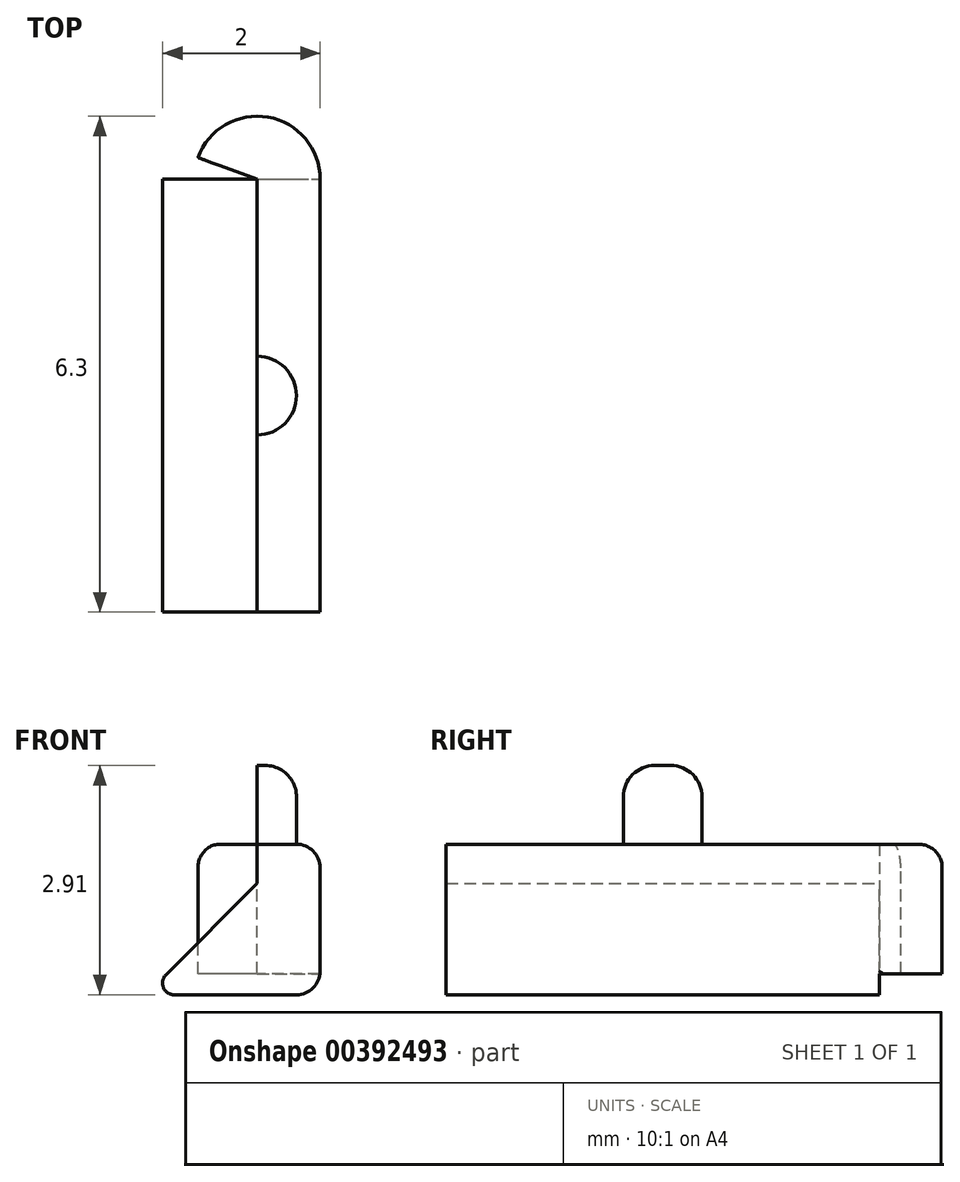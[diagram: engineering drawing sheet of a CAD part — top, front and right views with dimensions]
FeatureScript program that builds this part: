
annotation { "Feature Type Name" : "Feature", "Feature Type Description" : "" }
export const myFeature = defineFeature(function(context is Context, id is Id, definition is map)
    precondition{}
    {
        {
            var Q0;
            Q0=qCreatedBy(makeId("Front.planeOp"),FACE);
            var sketch = newSketch(context, id + "F0", { "sketchPlane" : qUnion([Q0])});
            skLineSegment(sketch, "E0", {"start": v(0.28, 1.82) * mm, "end": v(-1.14, 0.4) * mm});
            skLineSegment(sketch, "E1", {"start": v(-1.14, 0.4) * mm, "end": v(1.08, 0.4) * mm});
            skLineSegment(sketch, "E2", {"start": v(0.28, 1.82) * mm, "end": v(1.08, 1.82) * mm});
            skLineSegment(sketch, "E3", {"start": v(1.08, 1.82) * mm, "end": v(1.08, 0.4) * mm});
            skSolve(sketch);
        }
        {
            var Q0;
            Q0 = qSketchRegion(id + "F0", true);
            extrude(context, id + "F1", {"entities" : qUnion([Q0]), "depth" : 5.5 * mm});
        }
        {
            var Q0;
            Q0=makeQuery(id+"F1.opExtrude","SWEPT_FACE",FACE,{"disambiguationData":[OSD([sQuery(id+"F0.wireOp",EDGE,"E2")])]});
            var sketch = newSketch(context, id + "F2", { "sketchPlane" : qUnion([Q0])});
            skLineSegment(sketch, "E4", {"start": v(0.28, 0) * mm, "end": v(-0.47, 0.27) * mm});
            skArc(sketch, "E5", {"start": v(1.08, 0) * mm, "mid": v(0.42, 0.79) * mm, "end": v(-0.47, 0.27) * mm});
            skSolve(sketch);
        }
        {
            var Q0;
            Q0 = qSketchRegion(id + "F2", true);
            var Q1;
            Q1=makeQuery(id+"F2.imprint","IMPRINT",FACE,{"disambiguationData":[TD([[makeQuery(id+"F2.imprint","IMPRINT",EDGE,{"derivedFrom":sQuery(id+"F2.wireOp",EDGE,"E4")}),-1.0]])]});
            extrude(context, id + "F3", {"entities" : qUnion([Q0, Q1]), "operationType" : NewBodyOperationType.ADD, "oppositeDirection" : true, "depth" : 1.15 * mm});
        }
        {
            var Q0;
            Q0=makeQuery(id+"F1.opExtrude","SWEPT_EDGE",EDGE,{"disambiguationData":[OSD([sQuery(id+"F0.wireOp",EDGE,"E1"),sQuery(id+"F0.wireOp",EDGE,"E3")])]});
            fillet(context, id + "F4", {"entities" : qUnion([Q0]), "radius" : 0.3 * mm, "tangentPropagation" : true, "allowEdgeOverflow" : false});
        }
        {
            var Q0;
            Q0=makeQuery(id+"F1.opExtrude","SWEPT_EDGE",EDGE,{"disambiguationData":[OSD([sQuery(id+"F0.wireOp",EDGE,"E0"),sQuery(id+"F0.wireOp",EDGE,"E1")])]});
            fillet(context, id + "F5", {"entities" : qUnion([Q0]), "radius" : 0.15 * mm, "tangentPropagation" : true, "allowEdgeOverflow" : false});
        }
        {
            var Q0;
            {var subQ0=sQuery(id+"F0.wireOp",EDGE,"E2");Q0=makeQuery(id+"F3.boolean.opBoolean","MERGE",FACE,{"derivedFrom":[makeQuery(id+"F1.opExtrude","SWEPT_FACE",FACE,{"disambiguationData":[OSD([subQ0])]}),makeQuery(id+"F3.opExtrude","CAP_FACE",FACE,{"disambiguationData":[OSD([subQ0,sQuery(id+"F2.wireOp",EDGE,"E4"),sQuery(id+"F2.wireOp",EDGE,"E5")])],"isStart":true})]});}
            var sketch = newSketch(context, id + "F6", { "sketchPlane" : qUnion([Q0])});
            skPoint(sketch, "E6", {"position": v(0.28, -2.75) * mm});
            skCircle(sketch, "E7", {"center": v(0.28, -2.75) * mm, "radius": 0.5 * mm});
            skLineSegment(sketch, "E8", {"start": v(0.28, -2.25) * mm, "end": v(0.28, -3.25) * mm});
            skSolve(sketch);
        }
        {
            var Q0;
            {var subQ0=sQuery(id+"F6.wireOp",EDGE,"E8");Q0=makeQuery(id+"F6.imprint","IMPRINT",FACE,{"disambiguationData":[TD([[makeQuery(id+"F6.imprint","IMPRINT",EDGE,{"derivedFrom":subQ0}),-1.0]])]});}
            extrude(context, id + "F7", {"entities" : qUnion([Q0]), "operationType" : NewBodyOperationType.ADD, "depth" : 1.5 * mm, "hasSecondDirection" : true, "secondDirectionOppositeDirection" : true, "secondDirectionDepth" : 0.8 * mm});
        }
        {
            var Q0;
            Q0=makeQuery(id+"F7.opExtrude","CAP_EDGE",EDGE,{"disambiguationData":[OSD([sQuery(id+"F6.wireOp",EDGE,"E7")])],"isStart":false});
            fillet(context, id + "F8", {"entities" : qUnion([Q0]), "radius" : 0.4 * mm, "tangentPropagation" : true, "allowEdgeOverflow" : false});
        }
        {
            var Q0;
            {var subQ0=sQuery(id+"F0.wireOp",EDGE,"E2");var subQ1=makeQuery(id+"F3.opExtrude","CAP_FACE",FACE,{"disambiguationData":[OSD([subQ0,sQuery(id+"F2.wireOp",EDGE,"E4"),sQuery(id+"F2.wireOp",EDGE,"E5")])],"isStart":true});var subQ2=sQuery(id+"F0.wireOp",EDGE,"E3");var subQ3=sQuery(id+"F0.wireOp",EDGE,"E0");var subQ4=makeQuery(id+"F1.opExtrude","SWEPT_FACE",FACE,{"disambiguationData":[OSD([subQ0])]});Q0=makeQuery(id+"F7.boolean.opBoolean","SPLIT",FACE,{"disambiguationData":[TD([makeQuery(id+"F1.opExtrude","CAP_FACE",FACE,{"disambiguationData":[OSD([subQ3,sQuery(id+"F0.wireOp",EDGE,"E1"),subQ0,subQ2])],"isStart":false})])],"derivedFrom":makeQuery(id+"F3.boolean.opBoolean","MERGE",FACE,{"derivedFrom":[subQ4,subQ1]})});}
            var Q1;
            {var subQ0=sQuery(id+"F2.wireOp",EDGE,"E4");var subQ2=sQuery(id+"F0.wireOp",EDGE,"E2");var subQ4=makeQuery(id+"F1.opExtrude","SWEPT_FACE",FACE,{"disambiguationData":[OSD([subQ2])]});var subQ5=sQuery(id+"F2.wireOp",EDGE,"E5");var subQ6=makeQuery(id+"F3.opExtrude","CAP_FACE",FACE,{"disambiguationData":[OSD([subQ2,subQ0,subQ5])],"isStart":true});Q1=makeQuery(id+"F7.boolean.opBoolean","SPLIT",FACE,{"disambiguationData":[TD([makeQuery(id+"F3.opExtrude","SWEPT_FACE",FACE,{"disambiguationData":[OSD([subQ0])]})])],"derivedFrom":makeQuery(id+"F3.boolean.opBoolean","MERGE",FACE,{"derivedFrom":[subQ4,subQ6]})});}
            extrude(context, id + "F9", {"entities" : qUnion([Q0, Q1]), "operationType" : NewBodyOperationType.ADD, "depth" : 0.5 * mm});
        }
        {
            var Q0;
            Q0=makeQuery(id+"F9.opExtrude","CAP_EDGE",EDGE,{"disambiguationData":[OSD([sQuery(id+"F0.wireOp",EDGE,"E2"),sQuery(id+"F0.wireOp",EDGE,"E3")])],"isStart":false});
            fillet(context, id + "F10", {"entities" : qUnion([Q0]), "radius" : 0.3 * mm, "tangentPropagation" : true, "allowEdgeOverflow" : false});
        }
    });
